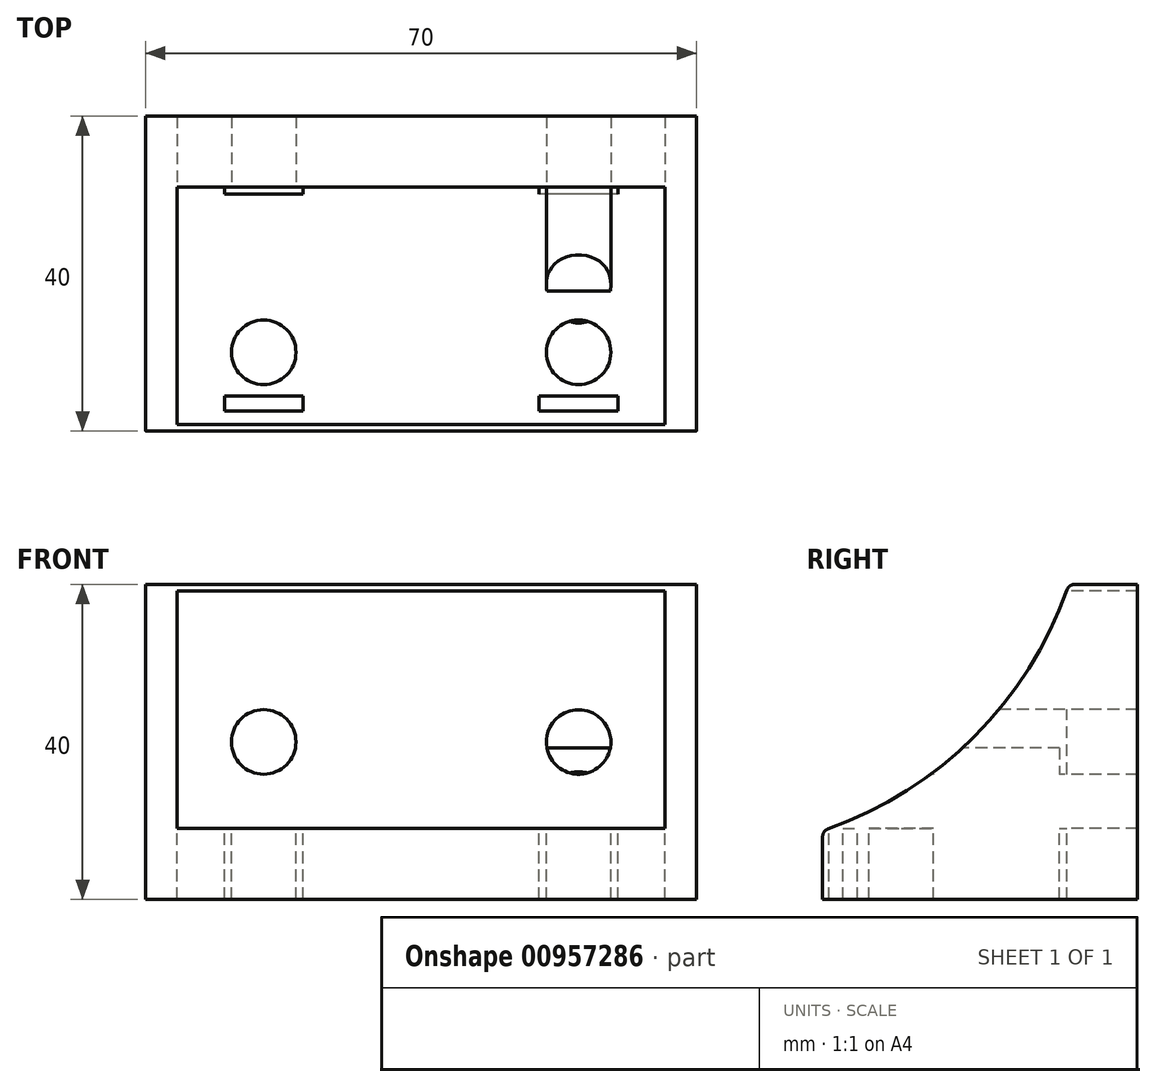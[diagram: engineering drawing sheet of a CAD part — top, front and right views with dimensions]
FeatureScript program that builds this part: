
annotation { "Feature Type Name" : "Feature", "Feature Type Description" : "" }
export const myFeature = defineFeature(function(context is Context, id is Id, definition is map)
    precondition{}
    {
        {
            var Q0;
            Q0=qCreatedBy(makeId("Right.planeOp"),FACE);
            var sketch = newSketch(context, id + "F0", { "sketchPlane" : qUnion([Q0])});
            skLineSegment(sketch, "E0", {"start": v(32.81, -19.75) * mm, "end": v(30.19, -19.75) * mm, "construction": true});
            skLineSegment(sketch, "E1", {"start": v(4.4, -19.75) * mm, "end": v(2.6, -19.75) * mm, "construction": true});
            skLineSegment(sketch, "E2", {"start": v(31, -3.35) * mm, "end": v(40, -3.35) * mm, "construction": true});
            skLineSegment(sketch, "E3", {"start": v(40, 4.85) * mm, "end": v(31, 4.85) * mm, "construction": true});
            skLineSegment(sketch, "E4", {"start": v(5.9, -10.25) * mm, "end": v(5.9, -19.25) * mm, "construction": true});
            skLineSegment(sketch, "E5", {"start": v(14.1, -19.25) * mm, "end": v(14.1, -10.25) * mm, "construction": true});
            skLineSegment(sketch, "E6", {"start": v(31, -10.25) * mm, "end": v(31, 19.92) * mm, "construction": true});
            skLineSegment(sketch, "E7", {"start": v(0.83, -10.25) * mm, "end": v(31, -10.25) * mm, "construction": true});
            skLineSegment(sketch, "E8", {"start": v(40.45, 0.75) * mm, "end": v(30.55, 0.75) * mm, "construction": true});
            skLineSegment(sketch, "E9", {"start": v(10, -19.7) * mm, "end": v(10, -9.8) * mm, "construction": true});
            skLineSegment(sketch, "E10", {"start": v(32.62, -20.84) * mm, "end": v(32.9, -19.25) * mm, "construction": true});
            skLineSegment(sketch, "E11", {"start": v(30.1, -19.25) * mm, "end": v(30.38, -20.84) * mm, "construction": true});
            skLineSegment(sketch, "E12", {"start": v(30.87, -21.25) * mm, "end": v(30.83, -21.25) * mm, "construction": true});
            skLineSegment(sketch, "E13", {"start": v(30.83, -21.25) * mm, "end": v(30.79, -21.24) * mm, "construction": true});
            skLineSegment(sketch, "E14", {"start": v(30.79, -21.24) * mm, "end": v(30.74, -21.23) * mm, "construction": true});
            skLineSegment(sketch, "E15", {"start": v(30.74, -21.23) * mm, "end": v(30.7, -21.22) * mm, "construction": true});
            skLineSegment(sketch, "E16", {"start": v(30.7, -21.22) * mm, "end": v(30.66, -21.2) * mm, "construction": true});
            skLineSegment(sketch, "E17", {"start": v(30.66, -21.2) * mm, "end": v(30.62, -21.18) * mm, "construction": true});
            skLineSegment(sketch, "E18", {"start": v(30.62, -21.18) * mm, "end": v(30.59, -21.16) * mm, "construction": true});
            skLineSegment(sketch, "E19", {"start": v(30.59, -21.16) * mm, "end": v(30.55, -21.13) * mm, "construction": true});
            skLineSegment(sketch, "E20", {"start": v(30.55, -21.13) * mm, "end": v(30.52, -21.1) * mm, "construction": true});
            skLineSegment(sketch, "E21", {"start": v(30.52, -21.1) * mm, "end": v(30.49, -21.07) * mm, "construction": true});
            skLineSegment(sketch, "E22", {"start": v(30.49, -21.07) * mm, "end": v(30.46, -21.04) * mm, "construction": true});
            skLineSegment(sketch, "E23", {"start": v(30.46, -21.04) * mm, "end": v(30.44, -21) * mm, "construction": true});
            skLineSegment(sketch, "E24", {"start": v(30.44, -21) * mm, "end": v(30.42, -20.96) * mm, "construction": true});
            skLineSegment(sketch, "E25", {"start": v(30.42, -20.96) * mm, "end": v(30.4, -20.92) * mm, "construction": true});
            skLineSegment(sketch, "E26", {"start": v(30.4, -20.92) * mm, "end": v(30.39, -20.88) * mm, "construction": true});
            skLineSegment(sketch, "E27", {"start": v(30.39, -20.88) * mm, "end": v(30.38, -20.84) * mm, "construction": true});
            skLineSegment(sketch, "E28", {"start": v(30.87, -21.25) * mm, "end": v(32.13, -21.25) * mm, "construction": true});
            skLineSegment(sketch, "E29", {"start": v(32.62, -20.84) * mm, "end": v(32.61, -20.88) * mm, "construction": true});
            skLineSegment(sketch, "E30", {"start": v(32.61, -20.88) * mm, "end": v(32.6, -20.92) * mm, "construction": true});
            skLineSegment(sketch, "E31", {"start": v(32.6, -20.92) * mm, "end": v(32.58, -20.96) * mm, "construction": true});
            skLineSegment(sketch, "E32", {"start": v(32.58, -20.96) * mm, "end": v(32.56, -21) * mm, "construction": true});
            skLineSegment(sketch, "E33", {"start": v(32.56, -21) * mm, "end": v(32.54, -21.04) * mm, "construction": true});
            skLineSegment(sketch, "E34", {"start": v(32.54, -21.04) * mm, "end": v(32.51, -21.07) * mm, "construction": true});
            skLineSegment(sketch, "E35", {"start": v(32.51, -21.07) * mm, "end": v(32.48, -21.1) * mm, "construction": true});
            skLineSegment(sketch, "E36", {"start": v(32.48, -21.1) * mm, "end": v(32.45, -21.13) * mm, "construction": true});
            skLineSegment(sketch, "E37", {"start": v(32.45, -21.13) * mm, "end": v(32.41, -21.16) * mm, "construction": true});
            skLineSegment(sketch, "E38", {"start": v(32.41, -21.16) * mm, "end": v(32.38, -21.18) * mm, "construction": true});
            skLineSegment(sketch, "E39", {"start": v(32.38, -21.18) * mm, "end": v(32.34, -21.2) * mm, "construction": true});
            skLineSegment(sketch, "E40", {"start": v(32.34, -21.2) * mm, "end": v(32.3, -21.22) * mm, "construction": true});
            skLineSegment(sketch, "E41", {"start": v(32.3, -21.22) * mm, "end": v(32.26, -21.23) * mm, "construction": true});
            skLineSegment(sketch, "E42", {"start": v(32.26, -21.23) * mm, "end": v(32.21, -21.24) * mm, "construction": true});
            skLineSegment(sketch, "E43", {"start": v(32.21, -21.24) * mm, "end": v(32.17, -21.25) * mm, "construction": true});
            skLineSegment(sketch, "E44", {"start": v(32.17, -21.25) * mm, "end": v(32.13, -21.25) * mm, "construction": true});
            skLineSegment(sketch, "E45", {"start": v(2.55, -19.25) * mm, "end": v(2.69, -20.8) * mm, "construction": true});
            skLineSegment(sketch, "E46", {"start": v(4.31, -20.8) * mm, "end": v(4.45, -19.25) * mm, "construction": true});
            skLineSegment(sketch, "E47", {"start": v(3.18, -21.25) * mm, "end": v(3.14, -21.25) * mm, "construction": true});
            skLineSegment(sketch, "E48", {"start": v(3.14, -21.25) * mm, "end": v(3.1, -21.24) * mm, "construction": true});
            skLineSegment(sketch, "E49", {"start": v(3.1, -21.24) * mm, "end": v(3.05, -21.23) * mm, "construction": true});
            skLineSegment(sketch, "E50", {"start": v(3.05, -21.23) * mm, "end": v(3.01, -21.22) * mm, "construction": true});
            skLineSegment(sketch, "E51", {"start": v(3.01, -21.22) * mm, "end": v(2.97, -21.2) * mm, "construction": true});
            skLineSegment(sketch, "E52", {"start": v(2.97, -21.2) * mm, "end": v(2.93, -21.18) * mm, "construction": true});
            skLineSegment(sketch, "E53", {"start": v(2.93, -21.18) * mm, "end": v(2.9, -21.16) * mm, "construction": true});
            skLineSegment(sketch, "E54", {"start": v(2.9, -21.16) * mm, "end": v(2.86, -21.13) * mm, "construction": true});
            skLineSegment(sketch, "E55", {"start": v(2.86, -21.13) * mm, "end": v(2.83, -21.1) * mm, "construction": true});
            skLineSegment(sketch, "E56", {"start": v(2.83, -21.1) * mm, "end": v(2.8, -21.07) * mm, "construction": true});
            skLineSegment(sketch, "E57", {"start": v(2.8, -21.07) * mm, "end": v(2.77, -21.04) * mm, "construction": true});
            skLineSegment(sketch, "E58", {"start": v(2.77, -21.04) * mm, "end": v(2.75, -21) * mm, "construction": true});
            skLineSegment(sketch, "E59", {"start": v(2.75, -21) * mm, "end": v(2.73, -20.96) * mm, "construction": true});
            skLineSegment(sketch, "E60", {"start": v(2.73, -20.96) * mm, "end": v(2.71, -20.92) * mm, "construction": true});
            skLineSegment(sketch, "E61", {"start": v(2.71, -20.92) * mm, "end": v(2.7, -20.88) * mm, "construction": true});
            skLineSegment(sketch, "E62", {"start": v(2.7, -20.88) * mm, "end": v(2.7, -20.84) * mm, "construction": true});
            skLineSegment(sketch, "E63", {"start": v(2.7, -20.84) * mm, "end": v(2.69, -20.8) * mm, "construction": true});
            skLineSegment(sketch, "E64", {"start": v(3.18, -21.25) * mm, "end": v(3.82, -21.25) * mm, "construction": true});
            skLineSegment(sketch, "E65", {"start": v(4.31, -20.8) * mm, "end": v(4.3, -20.84) * mm, "construction": true});
            skLineSegment(sketch, "E66", {"start": v(4.3, -20.84) * mm, "end": v(4.3, -20.88) * mm, "construction": true});
            skLineSegment(sketch, "E67", {"start": v(4.3, -20.88) * mm, "end": v(4.29, -20.92) * mm, "construction": true});
            skLineSegment(sketch, "E68", {"start": v(4.29, -20.92) * mm, "end": v(4.27, -20.96) * mm, "construction": true});
            skLineSegment(sketch, "E69", {"start": v(4.27, -20.96) * mm, "end": v(4.25, -21) * mm, "construction": true});
            skLineSegment(sketch, "E70", {"start": v(4.25, -21) * mm, "end": v(4.23, -21.04) * mm, "construction": true});
            skLineSegment(sketch, "E71", {"start": v(4.23, -21.04) * mm, "end": v(4.2, -21.07) * mm, "construction": true});
            skLineSegment(sketch, "E72", {"start": v(4.2, -21.07) * mm, "end": v(4.17, -21.1) * mm, "construction": true});
            skLineSegment(sketch, "E73", {"start": v(4.17, -21.1) * mm, "end": v(4.14, -21.13) * mm, "construction": true});
            skLineSegment(sketch, "E74", {"start": v(4.14, -21.13) * mm, "end": v(4.1, -21.16) * mm, "construction": true});
            skLineSegment(sketch, "E75", {"start": v(4.1, -21.16) * mm, "end": v(4.07, -21.18) * mm, "construction": true});
            skLineSegment(sketch, "E76", {"start": v(4.07, -21.18) * mm, "end": v(4.03, -21.2) * mm, "construction": true});
            skLineSegment(sketch, "E77", {"start": v(4.03, -21.2) * mm, "end": v(3.99, -21.22) * mm, "construction": true});
            skLineSegment(sketch, "E78", {"start": v(3.99, -21.22) * mm, "end": v(3.95, -21.23) * mm, "construction": true});
            skLineSegment(sketch, "E79", {"start": v(3.95, -21.23) * mm, "end": v(3.9, -21.24) * mm, "construction": true});
            skLineSegment(sketch, "E80", {"start": v(3.9, -21.24) * mm, "end": v(3.86, -21.25) * mm, "construction": true});
            skLineSegment(sketch, "E81", {"start": v(3.86, -21.25) * mm, "end": v(3.82, -21.25) * mm, "construction": true});
            skLineSegment(sketch, "E82", {"start": v(30.37, -20.78) * mm, "end": v(32.63, -20.78) * mm, "construction": true});
            skLineSegment(sketch, "E83", {"start": v(2.68, -20.78) * mm, "end": v(4.32, -20.78) * mm, "construction": true});
            skLineSegment(sketch, "E84", {"start": v(0, -11.25) * mm, "end": v(0, -19.25) * mm});
            skLineSegment(sketch, "E85", {"start": v(40, -19.25) * mm, "end": v(40, 20.75) * mm});
            skArc(sketch, "E86", {"start": v(0.67, -10.3) * mm, "mid": v(0.18, -10.67) * mm, "end": v(0, -11.25) * mm});
            skLineSegment(sketch, "E87", {"start": v(40, 20.75) * mm, "end": v(32, 20.75) * mm});
            skArc(sketch, "E88", {"start": v(32, 20.75) * mm, "mid": v(31.42, 20.57) * mm, "end": v(31.06, 20.08) * mm});
            skArc(sketch, "E89", {"start": v(0.67, -10.3) * mm, "mid": v(19.3, 1.46) * mm, "end": v(31.06, 20.08) * mm});
            skLineSegment(sketch, "E90", {"start": v(40, -19.25) * mm, "end": v(0, -19.25) * mm});
            skSolve(sketch);
        }
        {
            var Q0;
            Q0=makeQuery(id+"F0.imprint","IMPRINT",FACE,{"disambiguationData":[TD([[makeQuery(id+"F0.imprint","IMPRINT",EDGE,{"derivedFrom":sQuery(id+"F0.wireOp",EDGE,"E84")}),1.0]])]});
            extrude(context, id + "F1", {"entities" : qUnion([Q0]), "endBound" : BoundingType.SYMMETRIC, "depth" : 70 * mm, "offsetDistance" : 25 * mm});
        }
        {
            var Q0;
            Q0=qCreatedBy(makeId("Front.planeOp"),FACE);
            var sketch = newSketch(context, id + "F2", { "sketchPlane" : qUnion([Q0])});
            skLineSegment(sketch, "E91", {"start": v(17.26, -20.84) * mm, "end": v(15.09, -20.84) * mm});
            skLineSegment(sketch, "E92", {"start": v(22.7, -20.8) * mm, "end": v(22.74, -20.84) * mm});
            skLineSegment(sketch, "E93", {"start": v(17.26, -20.84) * mm, "end": v(17.3, -20.8) * mm});
            skLineSegment(sketch, "E94", {"start": v(24.91, -20.84) * mm, "end": v(22.74, -20.84) * mm});
            skLineSegment(sketch, "E95", {"start": v(-22.74, -20.84) * mm, "end": v(-24.91, -20.84) * mm});
            skLineSegment(sketch, "E96", {"start": v(-17.3, -20.8) * mm, "end": v(-17.26, -20.84) * mm});
            skLineSegment(sketch, "E97", {"start": v(-22.74, -20.84) * mm, "end": v(-22.7, -20.8) * mm});
            skLineSegment(sketch, "E98", {"start": v(-15.09, -20.84) * mm, "end": v(-17.26, -20.84) * mm});
            skLineSegment(sketch, "E99", {"start": v(-24.1, -10.25) * mm, "end": v(-24.1, -19.25) * mm});
            skLineSegment(sketch, "E100", {"start": v(-15.9, -19.25) * mm, "end": v(-15.9, -10.25) * mm});
            skLineSegment(sketch, "E101", {"start": v(15.9, -10.25) * mm, "end": v(15.9, -19.25) * mm});
            skLineSegment(sketch, "E102", {"start": v(24.1, -19.25) * mm, "end": v(24.1, -10.25) * mm});
            skLineSegment(sketch, "E103", {"start": v(-24.3, 0.75) * mm, "end": v(-15.7, 0.75) * mm, "construction": true});
            skLineSegment(sketch, "E104", {"start": v(-20, -3.55) * mm, "end": v(-20, 5.06) * mm, "construction": true});
            skLineSegment(sketch, "E105", {"start": v(15.7, 0.75) * mm, "end": v(24.3, 0.75) * mm, "construction": true});
            skLineSegment(sketch, "E106", {"start": v(20, -3.55) * mm, "end": v(20, 5.06) * mm, "construction": true});
            skLineSegment(sketch, "E107", {"start": v(20, -19.7) * mm, "end": v(20, -9.8) * mm});
            skLineSegment(sketch, "E108", {"start": v(-20, -19.7) * mm, "end": v(-20, -9.8) * mm});
            skLineSegment(sketch, "E109", {"start": v(35, 20.75) * mm, "end": v(-35, 20.75) * mm});
            skCircle(sketch, "E110", {"center": v(-20, 0.75) * mm, "radius": 4.1 * mm});
            skCircle(sketch, "E111", {"center": v(20, 0.75) * mm, "radius": 4.1 * mm});
            skLineSegment(sketch, "E112", {"start": v(23.12, -21.25) * mm, "end": v(23.1, -21.23) * mm});
            skLineSegment(sketch, "E113", {"start": v(23.1, -21.23) * mm, "end": v(23.06, -21.18) * mm});
            skLineSegment(sketch, "E114", {"start": v(23.06, -21.18) * mm, "end": v(23, -21.1) * mm});
            skLineSegment(sketch, "E115", {"start": v(23, -21.1) * mm, "end": v(22.85, -20.95) * mm});
            skLineSegment(sketch, "E116", {"start": v(22.85, -20.95) * mm, "end": v(22.7, -20.8) * mm});
            skLineSegment(sketch, "E117", {"start": v(24.42, -21.25) * mm, "end": v(24.46, -21.25) * mm});
            skLineSegment(sketch, "E118", {"start": v(24.46, -21.25) * mm, "end": v(24.5, -21.24) * mm});
            skLineSegment(sketch, "E119", {"start": v(24.5, -21.24) * mm, "end": v(24.55, -21.23) * mm});
            skLineSegment(sketch, "E120", {"start": v(24.55, -21.23) * mm, "end": v(24.6, -21.22) * mm});
            skLineSegment(sketch, "E121", {"start": v(24.6, -21.22) * mm, "end": v(24.63, -21.2) * mm});
            skLineSegment(sketch, "E122", {"start": v(24.63, -21.2) * mm, "end": v(24.67, -21.18) * mm});
            skLineSegment(sketch, "E123", {"start": v(24.67, -21.18) * mm, "end": v(24.7, -21.16) * mm});
            skLineSegment(sketch, "E124", {"start": v(24.7, -21.16) * mm, "end": v(24.74, -21.13) * mm});
            skLineSegment(sketch, "E125", {"start": v(24.74, -21.13) * mm, "end": v(24.77, -21.1) * mm});
            skLineSegment(sketch, "E126", {"start": v(24.77, -21.1) * mm, "end": v(24.8, -21.07) * mm});
            skLineSegment(sketch, "E127", {"start": v(24.8, -21.07) * mm, "end": v(24.83, -21.04) * mm});
            skLineSegment(sketch, "E128", {"start": v(24.83, -21.04) * mm, "end": v(24.85, -21) * mm});
            skLineSegment(sketch, "E129", {"start": v(24.85, -21) * mm, "end": v(24.87, -20.96) * mm});
            skLineSegment(sketch, "E130", {"start": v(24.87, -20.96) * mm, "end": v(24.9, -20.92) * mm});
            skLineSegment(sketch, "E131", {"start": v(24.9, -20.92) * mm, "end": v(24.9, -20.88) * mm});
            skLineSegment(sketch, "E132", {"start": v(24.9, -20.88) * mm, "end": v(24.91, -20.84) * mm});
            skLineSegment(sketch, "E133", {"start": v(24.91, -20.84) * mm, "end": v(24.92, -20.8) * mm});
            skLineSegment(sketch, "E134", {"start": v(24.42, -21.25) * mm, "end": v(23.12, -21.25) * mm});
            skLineSegment(sketch, "E135", {"start": v(-22.7, -20.8) * mm, "end": v(-22.87, -20.97) * mm});
            skLineSegment(sketch, "E136", {"start": v(-22.87, -20.97) * mm, "end": v(-23, -21.1) * mm});
            skLineSegment(sketch, "E137", {"start": v(-23, -21.1) * mm, "end": v(-23.08, -21.2) * mm});
            skLineSegment(sketch, "E138", {"start": v(-23.08, -21.2) * mm, "end": v(-23.11, -21.24) * mm});
            skLineSegment(sketch, "E139", {"start": v(-23.11, -21.24) * mm, "end": v(-23.12, -21.25) * mm});
            skLineSegment(sketch, "E140", {"start": v(-24.92, -20.8) * mm, "end": v(-24.91, -20.84) * mm});
            skLineSegment(sketch, "E141", {"start": v(-24.91, -20.84) * mm, "end": v(-24.9, -20.88) * mm});
            skLineSegment(sketch, "E142", {"start": v(-24.9, -20.88) * mm, "end": v(-24.9, -20.92) * mm});
            skLineSegment(sketch, "E143", {"start": v(-24.9, -20.92) * mm, "end": v(-24.87, -20.96) * mm});
            skLineSegment(sketch, "E144", {"start": v(-24.87, -20.96) * mm, "end": v(-24.85, -21) * mm});
            skLineSegment(sketch, "E145", {"start": v(-24.85, -21) * mm, "end": v(-24.83, -21.04) * mm});
            skLineSegment(sketch, "E146", {"start": v(-24.83, -21.04) * mm, "end": v(-24.8, -21.07) * mm});
            skLineSegment(sketch, "E147", {"start": v(-24.8, -21.07) * mm, "end": v(-24.77, -21.1) * mm});
            skLineSegment(sketch, "E148", {"start": v(-24.77, -21.1) * mm, "end": v(-24.74, -21.13) * mm});
            skLineSegment(sketch, "E149", {"start": v(-24.74, -21.13) * mm, "end": v(-24.7, -21.16) * mm});
            skLineSegment(sketch, "E150", {"start": v(-24.7, -21.16) * mm, "end": v(-24.67, -21.18) * mm});
            skLineSegment(sketch, "E151", {"start": v(-24.67, -21.18) * mm, "end": v(-24.63, -21.2) * mm});
            skLineSegment(sketch, "E152", {"start": v(-24.63, -21.2) * mm, "end": v(-24.6, -21.22) * mm});
            skLineSegment(sketch, "E153", {"start": v(-24.6, -21.22) * mm, "end": v(-24.55, -21.23) * mm});
            skLineSegment(sketch, "E154", {"start": v(-24.55, -21.23) * mm, "end": v(-24.5, -21.24) * mm});
            skLineSegment(sketch, "E155", {"start": v(-24.5, -21.24) * mm, "end": v(-24.46, -21.25) * mm});
            skLineSegment(sketch, "E156", {"start": v(-24.46, -21.25) * mm, "end": v(-24.42, -21.25) * mm});
            skLineSegment(sketch, "E157", {"start": v(-23.12, -21.25) * mm, "end": v(-24.42, -21.25) * mm});
            skLineSegment(sketch, "E158", {"start": v(-16.88, -21.25) * mm, "end": v(-16.9, -21.23) * mm});
            skLineSegment(sketch, "E159", {"start": v(-16.9, -21.23) * mm, "end": v(-16.94, -21.18) * mm});
            skLineSegment(sketch, "E160", {"start": v(-16.94, -21.18) * mm, "end": v(-17, -21.1) * mm});
            skLineSegment(sketch, "E161", {"start": v(-17, -21.1) * mm, "end": v(-17.15, -20.95) * mm});
            skLineSegment(sketch, "E162", {"start": v(-17.15, -20.95) * mm, "end": v(-17.3, -20.8) * mm});
            skLineSegment(sketch, "E163", {"start": v(-15.58, -21.25) * mm, "end": v(-15.54, -21.25) * mm});
            skLineSegment(sketch, "E164", {"start": v(-15.54, -21.25) * mm, "end": v(-15.5, -21.24) * mm});
            skLineSegment(sketch, "E165", {"start": v(-15.5, -21.24) * mm, "end": v(-15.45, -21.23) * mm});
            skLineSegment(sketch, "E166", {"start": v(-15.45, -21.23) * mm, "end": v(-15.4, -21.22) * mm});
            skLineSegment(sketch, "E167", {"start": v(-15.4, -21.22) * mm, "end": v(-15.37, -21.2) * mm});
            skLineSegment(sketch, "E168", {"start": v(-15.37, -21.2) * mm, "end": v(-15.33, -21.18) * mm});
            skLineSegment(sketch, "E169", {"start": v(-15.33, -21.18) * mm, "end": v(-15.3, -21.16) * mm});
            skLineSegment(sketch, "E170", {"start": v(-15.3, -21.16) * mm, "end": v(-15.26, -21.13) * mm});
            skLineSegment(sketch, "E171", {"start": v(-15.26, -21.13) * mm, "end": v(-15.23, -21.1) * mm});
            skLineSegment(sketch, "E172", {"start": v(-15.23, -21.1) * mm, "end": v(-15.2, -21.07) * mm});
            skLineSegment(sketch, "E173", {"start": v(-15.2, -21.07) * mm, "end": v(-15.17, -21.04) * mm});
            skLineSegment(sketch, "E174", {"start": v(-15.17, -21.04) * mm, "end": v(-15.15, -21) * mm});
            skLineSegment(sketch, "E175", {"start": v(-15.15, -21) * mm, "end": v(-15.13, -20.96) * mm});
            skLineSegment(sketch, "E176", {"start": v(-15.13, -20.96) * mm, "end": v(-15.1, -20.92) * mm});
            skLineSegment(sketch, "E177", {"start": v(-15.1, -20.92) * mm, "end": v(-15.1, -20.88) * mm});
            skLineSegment(sketch, "E178", {"start": v(-15.1, -20.88) * mm, "end": v(-15.09, -20.84) * mm});
            skLineSegment(sketch, "E179", {"start": v(-15.09, -20.84) * mm, "end": v(-15.08, -20.8) * mm});
            skLineSegment(sketch, "E180", {"start": v(-15.58, -21.25) * mm, "end": v(-16.88, -21.25) * mm});
            skLineSegment(sketch, "E181", {"start": v(17.3, -20.8) * mm, "end": v(17.13, -20.97) * mm});
            skLineSegment(sketch, "E182", {"start": v(17.13, -20.97) * mm, "end": v(17, -21.1) * mm});
            skLineSegment(sketch, "E183", {"start": v(17, -21.1) * mm, "end": v(16.92, -21.2) * mm});
            skLineSegment(sketch, "E184", {"start": v(16.92, -21.2) * mm, "end": v(16.89, -21.24) * mm});
            skLineSegment(sketch, "E185", {"start": v(16.89, -21.24) * mm, "end": v(16.88, -21.25) * mm});
            skLineSegment(sketch, "E186", {"start": v(15.08, -20.8) * mm, "end": v(15.09, -20.84) * mm});
            skLineSegment(sketch, "E187", {"start": v(15.09, -20.84) * mm, "end": v(15.1, -20.88) * mm});
            skLineSegment(sketch, "E188", {"start": v(15.1, -20.88) * mm, "end": v(15.1, -20.92) * mm});
            skLineSegment(sketch, "E189", {"start": v(15.1, -20.92) * mm, "end": v(15.13, -20.96) * mm});
            skLineSegment(sketch, "E190", {"start": v(15.13, -20.96) * mm, "end": v(15.15, -21) * mm});
            skLineSegment(sketch, "E191", {"start": v(15.15, -21) * mm, "end": v(15.17, -21.04) * mm});
            skLineSegment(sketch, "E192", {"start": v(15.17, -21.04) * mm, "end": v(15.2, -21.07) * mm});
            skLineSegment(sketch, "E193", {"start": v(15.2, -21.07) * mm, "end": v(15.23, -21.1) * mm});
            skLineSegment(sketch, "E194", {"start": v(15.23, -21.1) * mm, "end": v(15.26, -21.13) * mm});
            skLineSegment(sketch, "E195", {"start": v(15.26, -21.13) * mm, "end": v(15.3, -21.16) * mm});
            skLineSegment(sketch, "E196", {"start": v(15.3, -21.16) * mm, "end": v(15.33, -21.18) * mm});
            skLineSegment(sketch, "E197", {"start": v(15.33, -21.18) * mm, "end": v(15.37, -21.2) * mm});
            skLineSegment(sketch, "E198", {"start": v(15.37, -21.2) * mm, "end": v(15.4, -21.22) * mm});
            skLineSegment(sketch, "E199", {"start": v(15.4, -21.22) * mm, "end": v(15.45, -21.23) * mm});
            skLineSegment(sketch, "E200", {"start": v(15.45, -21.23) * mm, "end": v(15.5, -21.24) * mm});
            skLineSegment(sketch, "E201", {"start": v(15.5, -21.24) * mm, "end": v(15.54, -21.25) * mm});
            skLineSegment(sketch, "E202", {"start": v(15.54, -21.25) * mm, "end": v(15.58, -21.25) * mm});
            skLineSegment(sketch, "E203", {"start": v(16.88, -21.25) * mm, "end": v(15.58, -21.25) * mm});
            skLineSegment(sketch, "E204", {"start": v(24.92, -20.78) * mm, "end": v(24.92, -20.8) * mm});
            skLineSegment(sketch, "E205", {"start": v(24.92, -20.78) * mm, "end": v(25, -19.25) * mm});
            skLineSegment(sketch, "E206", {"start": v(15, -19.25) * mm, "end": v(15.08, -20.78) * mm});
            skLineSegment(sketch, "E207", {"start": v(15.08, -20.8) * mm, "end": v(15.08, -20.78) * mm});
            skLineSegment(sketch, "E208", {"start": v(17.3, -20.8) * mm, "end": v(15.08, -20.8) * mm});
            skLineSegment(sketch, "E209", {"start": v(17.3, -20.8) * mm, "end": v(17.57, -20.57) * mm});
            skLineSegment(sketch, "E210", {"start": v(17.57, -20.57) * mm, "end": v(17.86, -20.37) * mm});
            skLineSegment(sketch, "E211", {"start": v(17.86, -20.37) * mm, "end": v(18.16, -20.2) * mm});
            skLineSegment(sketch, "E212", {"start": v(18.16, -20.2) * mm, "end": v(18.48, -20.05) * mm});
            skLineSegment(sketch, "E213", {"start": v(18.48, -20.05) * mm, "end": v(18.8, -19.93) * mm});
            skLineSegment(sketch, "E214", {"start": v(18.8, -19.93) * mm, "end": v(19.14, -19.84) * mm});
            skLineSegment(sketch, "E215", {"start": v(19.14, -19.84) * mm, "end": v(19.49, -19.78) * mm});
            skLineSegment(sketch, "E216", {"start": v(19.49, -19.78) * mm, "end": v(19.84, -19.75) * mm});
            skLineSegment(sketch, "E217", {"start": v(19.84, -19.75) * mm, "end": v(20.19, -19.75) * mm});
            skLineSegment(sketch, "E218", {"start": v(20.19, -19.75) * mm, "end": v(20.53, -19.79) * mm});
            skLineSegment(sketch, "E219", {"start": v(20.53, -19.79) * mm, "end": v(20.88, -19.85) * mm});
            skLineSegment(sketch, "E220", {"start": v(20.88, -19.85) * mm, "end": v(21.21, -19.94) * mm});
            skLineSegment(sketch, "E221", {"start": v(21.21, -19.94) * mm, "end": v(21.54, -20.06) * mm});
            skLineSegment(sketch, "E222", {"start": v(21.54, -20.06) * mm, "end": v(21.86, -20.2) * mm});
            skLineSegment(sketch, "E223", {"start": v(21.86, -20.2) * mm, "end": v(22.16, -20.38) * mm});
            skLineSegment(sketch, "E224", {"start": v(22.16, -20.38) * mm, "end": v(22.44, -20.58) * mm});
            skLineSegment(sketch, "E225", {"start": v(22.44, -20.58) * mm, "end": v(22.7, -20.8) * mm});
            skLineSegment(sketch, "E226", {"start": v(24.92, -20.8) * mm, "end": v(22.7, -20.8) * mm});
            skLineSegment(sketch, "E227", {"start": v(-15.08, -20.78) * mm, "end": v(-15.08, -20.8) * mm});
            skLineSegment(sketch, "E228", {"start": v(-15.08, -20.78) * mm, "end": v(-15, -19.25) * mm});
            skLineSegment(sketch, "E229", {"start": v(-25, -19.25) * mm, "end": v(-24.92, -20.78) * mm});
            skLineSegment(sketch, "E230", {"start": v(-24.92, -20.8) * mm, "end": v(-24.92, -20.78) * mm});
            skLineSegment(sketch, "E231", {"start": v(-22.7, -20.8) * mm, "end": v(-24.92, -20.8) * mm});
            skLineSegment(sketch, "E232", {"start": v(-22.7, -20.8) * mm, "end": v(-22.43, -20.57) * mm});
            skLineSegment(sketch, "E233", {"start": v(-22.43, -20.57) * mm, "end": v(-22.14, -20.37) * mm});
            skLineSegment(sketch, "E234", {"start": v(-22.14, -20.37) * mm, "end": v(-21.84, -20.2) * mm});
            skLineSegment(sketch, "E235", {"start": v(-21.84, -20.2) * mm, "end": v(-21.52, -20.05) * mm});
            skLineSegment(sketch, "E236", {"start": v(-21.52, -20.05) * mm, "end": v(-21.2, -19.93) * mm});
            skLineSegment(sketch, "E237", {"start": v(-21.2, -19.93) * mm, "end": v(-20.86, -19.84) * mm});
            skLineSegment(sketch, "E238", {"start": v(-20.86, -19.84) * mm, "end": v(-20.51, -19.78) * mm});
            skLineSegment(sketch, "E239", {"start": v(-20.51, -19.78) * mm, "end": v(-20.16, -19.75) * mm});
            skLineSegment(sketch, "E240", {"start": v(-20.16, -19.75) * mm, "end": v(-19.81, -19.75) * mm});
            skLineSegment(sketch, "E241", {"start": v(-19.81, -19.75) * mm, "end": v(-19.47, -19.79) * mm});
            skLineSegment(sketch, "E242", {"start": v(-19.47, -19.79) * mm, "end": v(-19.12, -19.85) * mm});
            skLineSegment(sketch, "E243", {"start": v(-19.12, -19.85) * mm, "end": v(-18.79, -19.94) * mm});
            skLineSegment(sketch, "E244", {"start": v(-18.79, -19.94) * mm, "end": v(-18.46, -20.06) * mm});
            skLineSegment(sketch, "E245", {"start": v(-18.46, -20.06) * mm, "end": v(-18.14, -20.2) * mm});
            skLineSegment(sketch, "E246", {"start": v(-18.14, -20.2) * mm, "end": v(-17.84, -20.38) * mm});
            skLineSegment(sketch, "E247", {"start": v(-17.84, -20.38) * mm, "end": v(-17.56, -20.58) * mm});
            skLineSegment(sketch, "E248", {"start": v(-17.56, -20.58) * mm, "end": v(-17.3, -20.8) * mm});
            skLineSegment(sketch, "E249", {"start": v(-15.08, -20.8) * mm, "end": v(-17.3, -20.8) * mm});
            skLineSegment(sketch, "E250", {"start": v(31, -10.25) * mm, "end": v(31, 19.92) * mm});
            skLineSegment(sketch, "E251", {"start": v(31, -10.25) * mm, "end": v(-31, -10.25) * mm});
            skLineSegment(sketch, "E252", {"start": v(-31, -10.25) * mm, "end": v(-31, 19.92) * mm});
            skLineSegment(sketch, "E253", {"start": v(-31, 19.92) * mm, "end": v(31, 19.92) * mm});
            skLineSegment(sketch, "E254", {"start": v(35, 20.08) * mm, "end": v(-35, 20.08) * mm});
            skLineSegment(sketch, "E255", {"start": v(35, 20.75) * mm, "end": v(35, -19.25) * mm});
            skLineSegment(sketch, "E256", {"start": v(-35, 20.75) * mm, "end": v(-35, -19.25) * mm});
            skLineSegment(sketch, "E257", {"start": v(35, -19.25) * mm, "end": v(-35, -19.25) * mm});
            skLineSegment(sketch, "E258", {"start": v(35, -11.25) * mm, "end": v(-35, -11.25) * mm});
            skLineSegment(sketch, "E259", {"start": v(35, -10.3) * mm, "end": v(-35, -10.3) * mm});
            skSolve(sketch);
        }
        {
            var Q0;
            Q0=makeQuery(id+"F2.imprint","IMPRINT",FACE,{"disambiguationData":[TD([[makeQuery(id+"F2.imprint","IMPRINT",EDGE,{"derivedFrom":sQuery(id+"F2.wireOp",EDGE,"E110")}),1.0]])]});
            var Q1;
            Q1=makeQuery(id+"F2.imprint","IMPRINT",FACE,{"disambiguationData":[TD([[makeQuery(id+"F2.imprint","IMPRINT",EDGE,{"derivedFrom":sQuery(id+"F2.wireOp",EDGE,"E110")}),-1.0]])]});
            var Q2;
            Q2=makeQuery(id+"F2.imprint","IMPRINT",FACE,{"disambiguationData":[TD([[makeQuery(id+"F2.imprint","IMPRINT",EDGE,{"derivedFrom":sQuery(id+"F2.wireOp",EDGE,"E111")}),-1.0]])]});
            extrude(context, id + "F3", {"entities" : qUnion([Q0, Q1, Q2]), "operationType" : NewBodyOperationType.REMOVE, "oppositeDirection" : true, "depth" : 31 * mm, "offsetDistance" : 25 * mm});
        }
        {
            var Q0;
            Q0=makeQuery(id+"F2.imprint","IMPRINT",FACE,{"disambiguationData":[TD([[makeQuery(id+"F2.imprint","IMPRINT",EDGE,{"derivedFrom":sQuery(id+"F2.wireOp",EDGE,"E111")}),-1.0]])]});
            var Q1;
            Q1=makeQuery(id+"F2.imprint","IMPRINT",FACE,{"disambiguationData":[TD([[makeQuery(id+"F2.imprint","IMPRINT",EDGE,{"derivedFrom":sQuery(id+"F2.wireOp",EDGE,"E110")}),-1.0]])]});
            extrude(context, id + "F4", {"entities" : qUnion([Q0, Q1]), "operationType" : NewBodyOperationType.REMOVE, "endBound" : BoundingType.THROUGH_ALL, "oppositeDirection" : true, "depth" : 25 * mm, "offsetDistance" : 25 * mm});
        }
        {
            var Q0;
            Q0=qCreatedBy(makeId("Top.planeOp"),FACE);
            var sketch = newSketch(context, id + "F5", { "sketchPlane" : qUnion([Q0])});
            skLineSegment(sketch, "E260", {"start": v(23.12, 30.87) * mm, "end": v(23.12, 32.13) * mm});
            skLineSegment(sketch, "E261", {"start": v(24.42, 30.87) * mm, "end": v(24.42, 32.13) * mm});
            skLineSegment(sketch, "E262", {"start": v(24.42, 30.87) * mm, "end": v(23.12, 30.87) * mm});
            skLineSegment(sketch, "E263", {"start": v(24.42, 32.13) * mm, "end": v(23.12, 32.13) * mm});
            skLineSegment(sketch, "E264", {"start": v(-16.88, 30.87) * mm, "end": v(-16.88, 32.13) * mm});
            skLineSegment(sketch, "E265", {"start": v(-15.58, 30.87) * mm, "end": v(-15.58, 32.13) * mm});
            skLineSegment(sketch, "E266", {"start": v(-15.58, 30.87) * mm, "end": v(-16.88, 30.87) * mm});
            skLineSegment(sketch, "E267", {"start": v(-15.58, 32.13) * mm, "end": v(-16.88, 32.13) * mm});
            skLineSegment(sketch, "E268", {"start": v(-23.12, 30.87) * mm, "end": v(-23.12, 32.13) * mm});
            skLineSegment(sketch, "E269", {"start": v(-24.42, 30.87) * mm, "end": v(-24.42, 32.13) * mm});
            skLineSegment(sketch, "E270", {"start": v(-23.12, 30.87) * mm, "end": v(-24.42, 30.87) * mm});
            skLineSegment(sketch, "E271", {"start": v(-23.12, 32.13) * mm, "end": v(-24.42, 32.13) * mm});
            skLineSegment(sketch, "E272", {"start": v(16.88, 30.87) * mm, "end": v(16.88, 32.13) * mm});
            skLineSegment(sketch, "E273", {"start": v(15.58, 30.87) * mm, "end": v(15.58, 32.13) * mm});
            skLineSegment(sketch, "E274", {"start": v(16.88, 30.87) * mm, "end": v(15.58, 30.87) * mm});
            skLineSegment(sketch, "E275", {"start": v(16.88, 32.13) * mm, "end": v(15.58, 32.13) * mm});
            skLineSegment(sketch, "E276", {"start": v(23.12, 3.18) * mm, "end": v(23.12, 3.82) * mm});
            skLineSegment(sketch, "E277", {"start": v(24.42, 3.18) * mm, "end": v(24.42, 3.82) * mm});
            skLineSegment(sketch, "E278", {"start": v(24.42, 3.82) * mm, "end": v(23.12, 3.82) * mm});
            skLineSegment(sketch, "E279", {"start": v(24.42, 3.18) * mm, "end": v(23.12, 3.18) * mm});
            skLineSegment(sketch, "E280", {"start": v(-16.88, 3.18) * mm, "end": v(-16.88, 3.82) * mm});
            skLineSegment(sketch, "E281", {"start": v(-15.58, 3.18) * mm, "end": v(-15.58, 3.82) * mm});
            skLineSegment(sketch, "E282", {"start": v(-15.58, 3.82) * mm, "end": v(-16.88, 3.82) * mm});
            skLineSegment(sketch, "E283", {"start": v(-15.58, 3.18) * mm, "end": v(-16.88, 3.18) * mm});
            skLineSegment(sketch, "E284", {"start": v(-23.12, 3.18) * mm, "end": v(-23.12, 3.82) * mm});
            skLineSegment(sketch, "E285", {"start": v(-24.42, 3.18) * mm, "end": v(-24.42, 3.82) * mm});
            skLineSegment(sketch, "E286", {"start": v(-23.12, 3.82) * mm, "end": v(-24.42, 3.82) * mm});
            skLineSegment(sketch, "E287", {"start": v(-23.12, 3.18) * mm, "end": v(-24.42, 3.18) * mm});
            skLineSegment(sketch, "E288", {"start": v(16.88, 3.18) * mm, "end": v(16.88, 3.82) * mm});
            skLineSegment(sketch, "E289", {"start": v(15.58, 3.18) * mm, "end": v(15.58, 3.82) * mm});
            skLineSegment(sketch, "E290", {"start": v(16.88, 3.82) * mm, "end": v(15.58, 3.82) * mm});
            skLineSegment(sketch, "E291", {"start": v(16.88, 3.18) * mm, "end": v(15.58, 3.18) * mm});
            skLineSegment(sketch, "E292", {"start": v(-15.09, 32.62) * mm, "end": v(-17.26, 32.62) * mm});
            skLineSegment(sketch, "E293", {"start": v(-17.26, 32.62) * mm, "end": v(-17.09, 32.56) * mm});
            skLineSegment(sketch, "E294", {"start": v(-17.09, 32.56) * mm, "end": v(-16.98, 32.45) * mm});
            skLineSegment(sketch, "E295", {"start": v(-16.98, 32.45) * mm, "end": v(-16.91, 32.33) * mm});
            skLineSegment(sketch, "E296", {"start": v(-16.91, 32.33) * mm, "end": v(-16.88, 32.17) * mm});
            skLineSegment(sketch, "E297", {"start": v(-16.88, 32.17) * mm, "end": v(-16.88, 32.13) * mm});
            skLineSegment(sketch, "E298", {"start": v(-15.09, 32.62) * mm, "end": v(-15.58, 32.13) * mm});
            skLineSegment(sketch, "E299", {"start": v(24.91, 32.62) * mm, "end": v(22.74, 32.62) * mm});
            skLineSegment(sketch, "E300", {"start": v(22.74, 32.62) * mm, "end": v(22.91, 32.56) * mm});
            skLineSegment(sketch, "E301", {"start": v(22.91, 32.56) * mm, "end": v(23.02, 32.45) * mm});
            skLineSegment(sketch, "E302", {"start": v(23.02, 32.45) * mm, "end": v(23.09, 32.33) * mm});
            skLineSegment(sketch, "E303", {"start": v(23.09, 32.33) * mm, "end": v(23.12, 32.17) * mm});
            skLineSegment(sketch, "E304", {"start": v(23.12, 32.17) * mm, "end": v(23.12, 32.13) * mm});
            skLineSegment(sketch, "E305", {"start": v(24.91, 32.62) * mm, "end": v(24.42, 32.13) * mm});
            skLineSegment(sketch, "E306", {"start": v(-22.74, 32.62) * mm, "end": v(-24.91, 32.62) * mm});
            skLineSegment(sketch, "E307", {"start": v(-23.12, 32.13) * mm, "end": v(-23.1, 32.27) * mm});
            skLineSegment(sketch, "E308", {"start": v(-23.1, 32.27) * mm, "end": v(-23.06, 32.39) * mm});
            skLineSegment(sketch, "E309", {"start": v(-23.06, 32.39) * mm, "end": v(-23, 32.49) * mm});
            skLineSegment(sketch, "E310", {"start": v(-23, 32.49) * mm, "end": v(-22.86, 32.59) * mm});
            skLineSegment(sketch, "E311", {"start": v(-22.86, 32.59) * mm, "end": v(-22.74, 32.62) * mm});
            skLineSegment(sketch, "E312", {"start": v(-24.42, 32.13) * mm, "end": v(-24.91, 32.62) * mm});
            skLineSegment(sketch, "E313", {"start": v(17.26, 32.62) * mm, "end": v(15.09, 32.62) * mm});
            skLineSegment(sketch, "E314", {"start": v(16.88, 32.13) * mm, "end": v(16.9, 32.27) * mm});
            skLineSegment(sketch, "E315", {"start": v(16.9, 32.27) * mm, "end": v(16.94, 32.39) * mm});
            skLineSegment(sketch, "E316", {"start": v(16.94, 32.39) * mm, "end": v(17, 32.49) * mm});
            skLineSegment(sketch, "E317", {"start": v(17, 32.49) * mm, "end": v(17.14, 32.59) * mm});
            skLineSegment(sketch, "E318", {"start": v(17.14, 32.59) * mm, "end": v(17.26, 32.62) * mm});
            skLineSegment(sketch, "E319", {"start": v(15.58, 32.13) * mm, "end": v(15.09, 32.62) * mm});
            skLineSegment(sketch, "E320", {"start": v(24.91, 30.38) * mm, "end": v(22.74, 30.38) * mm});
            skLineSegment(sketch, "E321", {"start": v(23.12, 30.87) * mm, "end": v(23.1, 30.73) * mm});
            skLineSegment(sketch, "E322", {"start": v(23.1, 30.73) * mm, "end": v(23.06, 30.61) * mm});
            skLineSegment(sketch, "E323", {"start": v(23.06, 30.61) * mm, "end": v(23, 30.51) * mm});
            skLineSegment(sketch, "E324", {"start": v(23, 30.51) * mm, "end": v(22.86, 30.41) * mm});
            skLineSegment(sketch, "E325", {"start": v(22.86, 30.41) * mm, "end": v(22.74, 30.38) * mm});
            skLineSegment(sketch, "E326", {"start": v(24.42, 30.87) * mm, "end": v(24.91, 30.38) * mm});
            skLineSegment(sketch, "E327", {"start": v(-15.09, 30.38) * mm, "end": v(-17.26, 30.38) * mm});
            skLineSegment(sketch, "E328", {"start": v(-16.88, 30.87) * mm, "end": v(-16.9, 30.73) * mm});
            skLineSegment(sketch, "E329", {"start": v(-16.9, 30.73) * mm, "end": v(-16.94, 30.61) * mm});
            skLineSegment(sketch, "E330", {"start": v(-16.94, 30.61) * mm, "end": v(-17, 30.51) * mm});
            skLineSegment(sketch, "E331", {"start": v(-17, 30.51) * mm, "end": v(-17.14, 30.41) * mm});
            skLineSegment(sketch, "E332", {"start": v(-17.14, 30.41) * mm, "end": v(-17.26, 30.38) * mm});
            skLineSegment(sketch, "E333", {"start": v(-15.58, 30.87) * mm, "end": v(-15.09, 30.38) * mm});
            skLineSegment(sketch, "E334", {"start": v(-22.74, 30.38) * mm, "end": v(-24.91, 30.38) * mm});
            skLineSegment(sketch, "E335", {"start": v(-22.74, 30.38) * mm, "end": v(-22.91, 30.44) * mm});
            skLineSegment(sketch, "E336", {"start": v(-22.91, 30.44) * mm, "end": v(-23.02, 30.55) * mm});
            skLineSegment(sketch, "E337", {"start": v(-23.02, 30.55) * mm, "end": v(-23.09, 30.67) * mm});
            skLineSegment(sketch, "E338", {"start": v(-23.09, 30.67) * mm, "end": v(-23.12, 30.83) * mm});
            skLineSegment(sketch, "E339", {"start": v(-23.12, 30.83) * mm, "end": v(-23.12, 30.87) * mm});
            skLineSegment(sketch, "E340", {"start": v(-24.91, 30.38) * mm, "end": v(-24.42, 30.87) * mm});
            skLineSegment(sketch, "E341", {"start": v(17.26, 30.38) * mm, "end": v(15.09, 30.38) * mm});
            skLineSegment(sketch, "E342", {"start": v(17.26, 30.38) * mm, "end": v(17.09, 30.44) * mm});
            skLineSegment(sketch, "E343", {"start": v(17.09, 30.44) * mm, "end": v(16.98, 30.55) * mm});
            skLineSegment(sketch, "E344", {"start": v(16.98, 30.55) * mm, "end": v(16.91, 30.67) * mm});
            skLineSegment(sketch, "E345", {"start": v(16.91, 30.67) * mm, "end": v(16.88, 30.83) * mm});
            skLineSegment(sketch, "E346", {"start": v(16.88, 30.83) * mm, "end": v(16.88, 30.87) * mm});
            skLineSegment(sketch, "E347", {"start": v(15.09, 30.38) * mm, "end": v(15.58, 30.87) * mm});
            skLineSegment(sketch, "E348", {"start": v(-22.7, 2.69) * mm, "end": v(-24.92, 2.69) * mm});
            skLineSegment(sketch, "E349", {"start": v(-22.7, 2.69) * mm, "end": v(-22.87, 2.73) * mm});
            skLineSegment(sketch, "E350", {"start": v(-22.87, 2.73) * mm, "end": v(-23, 2.83) * mm});
            skLineSegment(sketch, "E351", {"start": v(-23, 2.83) * mm, "end": v(-23.08, 2.95) * mm});
            skLineSegment(sketch, "E352", {"start": v(-23.08, 2.95) * mm, "end": v(-23.11, 3.08) * mm});
            skLineSegment(sketch, "E353", {"start": v(-23.11, 3.08) * mm, "end": v(-23.12, 3.18) * mm});
            skLineSegment(sketch, "E354", {"start": v(-24.92, 2.69) * mm, "end": v(-24.42, 3.18) * mm});
            skLineSegment(sketch, "E355", {"start": v(17.3, 2.69) * mm, "end": v(15.08, 2.69) * mm});
            skLineSegment(sketch, "E356", {"start": v(17.3, 2.69) * mm, "end": v(17.13, 2.73) * mm});
            skLineSegment(sketch, "E357", {"start": v(17.13, 2.73) * mm, "end": v(17, 2.83) * mm});
            skLineSegment(sketch, "E358", {"start": v(17, 2.83) * mm, "end": v(16.92, 2.95) * mm});
            skLineSegment(sketch, "E359", {"start": v(16.92, 2.95) * mm, "end": v(16.89, 3.08) * mm});
            skLineSegment(sketch, "E360", {"start": v(16.89, 3.08) * mm, "end": v(16.88, 3.18) * mm});
            skLineSegment(sketch, "E361", {"start": v(15.08, 2.69) * mm, "end": v(15.58, 3.18) * mm});
            skLineSegment(sketch, "E362", {"start": v(24.92, 2.69) * mm, "end": v(22.7, 2.69) * mm});
            skLineSegment(sketch, "E363", {"start": v(23.12, 3.18) * mm, "end": v(23.1, 3.05) * mm});
            skLineSegment(sketch, "E364", {"start": v(23.1, 3.05) * mm, "end": v(23.06, 2.92) * mm});
            skLineSegment(sketch, "E365", {"start": v(23.06, 2.92) * mm, "end": v(23, 2.82) * mm});
            skLineSegment(sketch, "E366", {"start": v(23, 2.82) * mm, "end": v(22.86, 2.72) * mm});
            skLineSegment(sketch, "E367", {"start": v(22.86, 2.72) * mm, "end": v(22.7, 2.69) * mm});
            skLineSegment(sketch, "E368", {"start": v(24.42, 3.18) * mm, "end": v(24.92, 2.69) * mm});
            skLineSegment(sketch, "E369", {"start": v(-15.08, 2.69) * mm, "end": v(-17.3, 2.69) * mm});
            skLineSegment(sketch, "E370", {"start": v(-16.88, 3.18) * mm, "end": v(-16.9, 3.05) * mm});
            skLineSegment(sketch, "E371", {"start": v(-16.9, 3.05) * mm, "end": v(-16.94, 2.92) * mm});
            skLineSegment(sketch, "E372", {"start": v(-16.94, 2.92) * mm, "end": v(-17, 2.82) * mm});
            skLineSegment(sketch, "E373", {"start": v(-17, 2.82) * mm, "end": v(-17.14, 2.72) * mm});
            skLineSegment(sketch, "E374", {"start": v(-17.14, 2.72) * mm, "end": v(-17.3, 2.69) * mm});
            skLineSegment(sketch, "E375", {"start": v(-15.58, 3.18) * mm, "end": v(-15.08, 2.69) * mm});
            skLineSegment(sketch, "E376", {"start": v(17.3, 4.31) * mm, "end": v(15.08, 4.31) * mm});
            skLineSegment(sketch, "E377", {"start": v(16.88, 3.82) * mm, "end": v(16.9, 3.95) * mm});
            skLineSegment(sketch, "E378", {"start": v(16.9, 3.95) * mm, "end": v(16.94, 4.08) * mm});
            skLineSegment(sketch, "E379", {"start": v(16.94, 4.08) * mm, "end": v(17, 4.18) * mm});
            skLineSegment(sketch, "E380", {"start": v(17, 4.18) * mm, "end": v(17.14, 4.28) * mm});
            skLineSegment(sketch, "E381", {"start": v(17.14, 4.28) * mm, "end": v(17.3, 4.31) * mm});
            skLineSegment(sketch, "E382", {"start": v(15.58, 3.82) * mm, "end": v(15.08, 4.31) * mm});
            skLineSegment(sketch, "E383", {"start": v(-15.08, 4.31) * mm, "end": v(-17.3, 4.31) * mm});
            skLineSegment(sketch, "E384", {"start": v(-17.3, 4.31) * mm, "end": v(-17.13, 4.27) * mm});
            skLineSegment(sketch, "E385", {"start": v(-17.13, 4.27) * mm, "end": v(-17, 4.17) * mm});
            skLineSegment(sketch, "E386", {"start": v(-17, 4.17) * mm, "end": v(-16.92, 4.05) * mm});
            skLineSegment(sketch, "E387", {"start": v(-16.92, 4.05) * mm, "end": v(-16.89, 3.92) * mm});
            skLineSegment(sketch, "E388", {"start": v(-16.89, 3.92) * mm, "end": v(-16.88, 3.82) * mm});
            skLineSegment(sketch, "E389", {"start": v(-15.08, 4.31) * mm, "end": v(-15.58, 3.82) * mm});
            skLineSegment(sketch, "E390", {"start": v(24.92, 4.31) * mm, "end": v(22.7, 4.31) * mm});
            skLineSegment(sketch, "E391", {"start": v(22.7, 4.31) * mm, "end": v(22.87, 4.27) * mm});
            skLineSegment(sketch, "E392", {"start": v(22.87, 4.27) * mm, "end": v(23, 4.17) * mm});
            skLineSegment(sketch, "E393", {"start": v(23, 4.17) * mm, "end": v(23.08, 4.05) * mm});
            skLineSegment(sketch, "E394", {"start": v(23.08, 4.05) * mm, "end": v(23.11, 3.92) * mm});
            skLineSegment(sketch, "E395", {"start": v(23.11, 3.92) * mm, "end": v(23.12, 3.82) * mm});
            skLineSegment(sketch, "E396", {"start": v(24.92, 4.31) * mm, "end": v(24.42, 3.82) * mm});
            skLineSegment(sketch, "E397", {"start": v(-22.7, 4.31) * mm, "end": v(-24.92, 4.31) * mm});
            skLineSegment(sketch, "E398", {"start": v(-23.12, 3.82) * mm, "end": v(-23.1, 3.95) * mm});
            skLineSegment(sketch, "E399", {"start": v(-23.1, 3.95) * mm, "end": v(-23.06, 4.08) * mm});
            skLineSegment(sketch, "E400", {"start": v(-23.06, 4.08) * mm, "end": v(-23, 4.18) * mm});
            skLineSegment(sketch, "E401", {"start": v(-23, 4.18) * mm, "end": v(-22.86, 4.28) * mm});
            skLineSegment(sketch, "E402", {"start": v(-22.86, 4.28) * mm, "end": v(-22.7, 4.31) * mm});
            skLineSegment(sketch, "E403", {"start": v(-24.42, 3.82) * mm, "end": v(-24.92, 4.31) * mm});
            skLineSegment(sketch, "E404", {"start": v(15.09, 30.38) * mm, "end": v(15.08, 30.37) * mm});
            skLineSegment(sketch, "E405", {"start": v(15.08, 30.37) * mm, "end": v(15.08, 30.37) * mm});
            skLineSegment(sketch, "E406", {"start": v(15.08, 32.63) * mm, "end": v(15.08, 32.62) * mm});
            skLineSegment(sketch, "E407", {"start": v(15.08, 32.62) * mm, "end": v(15.09, 32.62) * mm});
            skLineSegment(sketch, "E408", {"start": v(15.08, 30.37) * mm, "end": v(15.08, 32.63) * mm});
            skLineSegment(sketch, "E409", {"start": v(-15.08, 30.37) * mm, "end": v(-15.08, 30.38) * mm});
            skLineSegment(sketch, "E410", {"start": v(-15.08, 30.38) * mm, "end": v(-15.09, 30.38) * mm});
            skLineSegment(sketch, "E411", {"start": v(-15.08, 30.37) * mm, "end": v(-15.08, 32.63) * mm});
            skLineSegment(sketch, "E412", {"start": v(-15.09, 32.62) * mm, "end": v(-15.08, 32.63) * mm});
            skLineSegment(sketch, "E413", {"start": v(-15.08, 32.63) * mm, "end": v(-15.08, 32.63) * mm});
            skLineSegment(sketch, "E414", {"start": v(24.92, 30.37) * mm, "end": v(24.92, 32.63) * mm});
            skLineSegment(sketch, "E415", {"start": v(24.92, 30.37) * mm, "end": v(24.92, 30.38) * mm});
            skLineSegment(sketch, "E416", {"start": v(24.92, 30.38) * mm, "end": v(24.91, 30.38) * mm});
            skLineSegment(sketch, "E417", {"start": v(24.91, 32.62) * mm, "end": v(24.92, 32.63) * mm});
            skLineSegment(sketch, "E418", {"start": v(24.92, 32.63) * mm, "end": v(24.92, 32.63) * mm});
            skLineSegment(sketch, "E419", {"start": v(-24.91, 30.38) * mm, "end": v(-24.92, 30.37) * mm});
            skLineSegment(sketch, "E420", {"start": v(-24.92, 30.37) * mm, "end": v(-24.92, 30.37) * mm});
            skLineSegment(sketch, "E421", {"start": v(-24.92, 32.63) * mm, "end": v(-24.92, 32.62) * mm});
            skLineSegment(sketch, "E422", {"start": v(-24.92, 32.62) * mm, "end": v(-24.91, 32.62) * mm});
            skLineSegment(sketch, "E423", {"start": v(-24.92, 30.37) * mm, "end": v(-24.92, 32.63) * mm});
            skLineSegment(sketch, "E424", {"start": v(15.08, 2.69) * mm, "end": v(15.08, 2.68) * mm});
            skLineSegment(sketch, "E425", {"start": v(15.08, 4.32) * mm, "end": v(15.08, 4.31) * mm});
            skLineSegment(sketch, "E426", {"start": v(15.08, 2.68) * mm, "end": v(15.08, 4.32) * mm});
            skLineSegment(sketch, "E427", {"start": v(24.92, 2.68) * mm, "end": v(24.92, 4.32) * mm});
            skLineSegment(sketch, "E428", {"start": v(24.92, 2.68) * mm, "end": v(24.92, 2.69) * mm});
            skLineSegment(sketch, "E429", {"start": v(24.92, 4.31) * mm, "end": v(24.92, 4.32) * mm});
            skLineSegment(sketch, "E430", {"start": v(-15.08, 2.68) * mm, "end": v(-15.08, 2.69) * mm});
            skLineSegment(sketch, "E431", {"start": v(-15.08, 2.68) * mm, "end": v(-15.08, 4.32) * mm});
            skLineSegment(sketch, "E432", {"start": v(-15.08, 4.31) * mm, "end": v(-15.08, 4.32) * mm});
            skLineSegment(sketch, "E433", {"start": v(-24.92, 2.69) * mm, "end": v(-24.92, 2.68) * mm});
            skLineSegment(sketch, "E434", {"start": v(-24.92, 4.32) * mm, "end": v(-24.92, 4.31) * mm});
            skLineSegment(sketch, "E435", {"start": v(-24.92, 2.68) * mm, "end": v(-24.92, 4.32) * mm});
            skLineSegment(sketch, "E436", {"start": v(17.26, 30.38) * mm, "end": v(17.52, 30.34) * mm});
            skLineSegment(sketch, "E437", {"start": v(17.52, 30.34) * mm, "end": v(17.8, 30.3) * mm});
            skLineSegment(sketch, "E438", {"start": v(17.8, 30.3) * mm, "end": v(18.1, 30.27) * mm});
            skLineSegment(sketch, "E439", {"start": v(18.1, 30.27) * mm, "end": v(18.42, 30.25) * mm});
            skLineSegment(sketch, "E440", {"start": v(18.42, 30.25) * mm, "end": v(18.75, 30.22) * mm});
            skLineSegment(sketch, "E441", {"start": v(18.75, 30.22) * mm, "end": v(19.08, 30.2) * mm});
            skLineSegment(sketch, "E442", {"start": v(19.08, 30.2) * mm, "end": v(19.43, 30.2) * mm});
            skLineSegment(sketch, "E443", {"start": v(19.43, 30.2) * mm, "end": v(19.77, 30.19) * mm});
            skLineSegment(sketch, "E444", {"start": v(19.77, 30.19) * mm, "end": v(20.12, 30.19) * mm});
            skLineSegment(sketch, "E445", {"start": v(20.12, 30.19) * mm, "end": v(20.47, 30.2) * mm});
            skLineSegment(sketch, "E446", {"start": v(20.47, 30.2) * mm, "end": v(20.81, 30.2) * mm});
            skLineSegment(sketch, "E447", {"start": v(20.81, 30.2) * mm, "end": v(21.15, 30.22) * mm});
            skLineSegment(sketch, "E448", {"start": v(21.15, 30.22) * mm, "end": v(21.48, 30.24) * mm});
            skLineSegment(sketch, "E449", {"start": v(21.48, 30.24) * mm, "end": v(21.8, 30.26) * mm});
            skLineSegment(sketch, "E450", {"start": v(21.8, 30.26) * mm, "end": v(22.1, 30.3) * mm});
            skLineSegment(sketch, "E451", {"start": v(22.1, 30.3) * mm, "end": v(22.4, 30.33) * mm});
            skLineSegment(sketch, "E452", {"start": v(22.4, 30.33) * mm, "end": v(22.66, 30.37) * mm});
            skLineSegment(sketch, "E453", {"start": v(22.66, 30.37) * mm, "end": v(22.74, 30.38) * mm});
            skLineSegment(sketch, "E454", {"start": v(22.74, 32.62) * mm, "end": v(22.48, 32.66) * mm});
            skLineSegment(sketch, "E455", {"start": v(22.48, 32.66) * mm, "end": v(22.2, 32.7) * mm});
            skLineSegment(sketch, "E456", {"start": v(22.2, 32.7) * mm, "end": v(21.9, 32.73) * mm});
            skLineSegment(sketch, "E457", {"start": v(21.9, 32.73) * mm, "end": v(21.58, 32.75) * mm});
            skLineSegment(sketch, "E458", {"start": v(21.58, 32.75) * mm, "end": v(21.25, 32.78) * mm});
            skLineSegment(sketch, "E459", {"start": v(21.25, 32.78) * mm, "end": v(20.92, 32.8) * mm});
            skLineSegment(sketch, "E460", {"start": v(20.92, 32.8) * mm, "end": v(20.57, 32.8) * mm});
            skLineSegment(sketch, "E461", {"start": v(20.57, 32.8) * mm, "end": v(20.23, 32.81) * mm});
            skLineSegment(sketch, "E462", {"start": v(20.23, 32.81) * mm, "end": v(19.88, 32.81) * mm});
            skLineSegment(sketch, "E463", {"start": v(19.88, 32.81) * mm, "end": v(19.53, 32.8) * mm});
            skLineSegment(sketch, "E464", {"start": v(19.53, 32.8) * mm, "end": v(19.19, 32.8) * mm});
            skLineSegment(sketch, "E465", {"start": v(19.19, 32.8) * mm, "end": v(18.85, 32.78) * mm});
            skLineSegment(sketch, "E466", {"start": v(18.85, 32.78) * mm, "end": v(18.52, 32.76) * mm});
            skLineSegment(sketch, "E467", {"start": v(18.52, 32.76) * mm, "end": v(18.2, 32.74) * mm});
            skLineSegment(sketch, "E468", {"start": v(18.2, 32.74) * mm, "end": v(17.9, 32.7) * mm});
            skLineSegment(sketch, "E469", {"start": v(17.9, 32.7) * mm, "end": v(17.6, 32.67) * mm});
            skLineSegment(sketch, "E470", {"start": v(17.6, 32.67) * mm, "end": v(17.34, 32.63) * mm});
            skLineSegment(sketch, "E471", {"start": v(17.34, 32.63) * mm, "end": v(17.26, 32.62) * mm});
            skLineSegment(sketch, "E472", {"start": v(17.3, 2.69) * mm, "end": v(17.57, 2.67) * mm});
            skLineSegment(sketch, "E473", {"start": v(17.57, 2.67) * mm, "end": v(17.86, 2.65) * mm});
            skLineSegment(sketch, "E474", {"start": v(17.86, 2.65) * mm, "end": v(18.16, 2.63) * mm});
            skLineSegment(sketch, "E475", {"start": v(18.16, 2.63) * mm, "end": v(18.48, 2.62) * mm});
            skLineSegment(sketch, "E476", {"start": v(18.48, 2.62) * mm, "end": v(18.8, 2.6) * mm});
            skLineSegment(sketch, "E477", {"start": v(18.8, 2.6) * mm, "end": v(19.14, 2.6) * mm});
            skLineSegment(sketch, "E478", {"start": v(19.14, 2.6) * mm, "end": v(19.49, 2.6) * mm});
            skLineSegment(sketch, "E479", {"start": v(19.49, 2.6) * mm, "end": v(19.84, 2.6) * mm});
            skLineSegment(sketch, "E480", {"start": v(19.84, 2.6) * mm, "end": v(20.19, 2.6) * mm});
            skLineSegment(sketch, "E481", {"start": v(20.19, 2.6) * mm, "end": v(20.53, 2.6) * mm});
            skLineSegment(sketch, "E482", {"start": v(20.53, 2.6) * mm, "end": v(20.88, 2.6) * mm});
            skLineSegment(sketch, "E483", {"start": v(20.88, 2.6) * mm, "end": v(21.21, 2.61) * mm});
            skLineSegment(sketch, "E484", {"start": v(21.21, 2.61) * mm, "end": v(21.54, 2.62) * mm});
            skLineSegment(sketch, "E485", {"start": v(21.54, 2.62) * mm, "end": v(21.86, 2.63) * mm});
            skLineSegment(sketch, "E486", {"start": v(21.86, 2.63) * mm, "end": v(22.16, 2.65) * mm});
            skLineSegment(sketch, "E487", {"start": v(22.16, 2.65) * mm, "end": v(22.44, 2.67) * mm});
            skLineSegment(sketch, "E488", {"start": v(22.44, 2.67) * mm, "end": v(22.7, 2.69) * mm});
            skLineSegment(sketch, "E489", {"start": v(22.7, 4.31) * mm, "end": v(22.43, 4.33) * mm});
            skLineSegment(sketch, "E490", {"start": v(22.43, 4.33) * mm, "end": v(22.14, 4.35) * mm});
            skLineSegment(sketch, "E491", {"start": v(22.14, 4.35) * mm, "end": v(21.84, 4.37) * mm});
            skLineSegment(sketch, "E492", {"start": v(21.84, 4.37) * mm, "end": v(21.52, 4.38) * mm});
            skLineSegment(sketch, "E493", {"start": v(21.52, 4.38) * mm, "end": v(21.2, 4.4) * mm});
            skLineSegment(sketch, "E494", {"start": v(21.2, 4.4) * mm, "end": v(20.86, 4.4) * mm});
            skLineSegment(sketch, "E495", {"start": v(20.86, 4.4) * mm, "end": v(20.51, 4.4) * mm});
            skLineSegment(sketch, "E496", {"start": v(20.51, 4.4) * mm, "end": v(20.16, 4.4) * mm});
            skLineSegment(sketch, "E497", {"start": v(20.16, 4.4) * mm, "end": v(19.81, 4.4) * mm});
            skLineSegment(sketch, "E498", {"start": v(19.81, 4.4) * mm, "end": v(19.47, 4.4) * mm});
            skLineSegment(sketch, "E499", {"start": v(19.47, 4.4) * mm, "end": v(19.12, 4.4) * mm});
            skLineSegment(sketch, "E500", {"start": v(19.12, 4.4) * mm, "end": v(18.79, 4.39) * mm});
            skLineSegment(sketch, "E501", {"start": v(18.79, 4.39) * mm, "end": v(18.46, 4.38) * mm});
            skLineSegment(sketch, "E502", {"start": v(18.46, 4.38) * mm, "end": v(18.14, 4.37) * mm});
            skLineSegment(sketch, "E503", {"start": v(18.14, 4.37) * mm, "end": v(17.84, 4.35) * mm});
            skLineSegment(sketch, "E504", {"start": v(17.84, 4.35) * mm, "end": v(17.56, 4.33) * mm});
            skLineSegment(sketch, "E505", {"start": v(17.56, 4.33) * mm, "end": v(17.3, 4.31) * mm});
            skLineSegment(sketch, "E506", {"start": v(-22.74, 30.38) * mm, "end": v(-22.48, 30.34) * mm});
            skLineSegment(sketch, "E507", {"start": v(-22.48, 30.34) * mm, "end": v(-22.2, 30.3) * mm});
            skLineSegment(sketch, "E508", {"start": v(-22.2, 30.3) * mm, "end": v(-21.9, 30.27) * mm});
            skLineSegment(sketch, "E509", {"start": v(-21.9, 30.27) * mm, "end": v(-21.58, 30.25) * mm});
            skLineSegment(sketch, "E510", {"start": v(-21.58, 30.25) * mm, "end": v(-21.25, 30.22) * mm});
            skLineSegment(sketch, "E511", {"start": v(-21.25, 30.22) * mm, "end": v(-20.92, 30.2) * mm});
            skLineSegment(sketch, "E512", {"start": v(-20.92, 30.2) * mm, "end": v(-20.57, 30.2) * mm});
            skLineSegment(sketch, "E513", {"start": v(-20.57, 30.2) * mm, "end": v(-20.23, 30.19) * mm});
            skLineSegment(sketch, "E514", {"start": v(-20.23, 30.19) * mm, "end": v(-19.88, 30.19) * mm});
            skLineSegment(sketch, "E515", {"start": v(-19.88, 30.19) * mm, "end": v(-19.53, 30.2) * mm});
            skLineSegment(sketch, "E516", {"start": v(-19.53, 30.2) * mm, "end": v(-19.19, 30.2) * mm});
            skLineSegment(sketch, "E517", {"start": v(-19.19, 30.2) * mm, "end": v(-18.85, 30.22) * mm});
            skLineSegment(sketch, "E518", {"start": v(-18.85, 30.22) * mm, "end": v(-18.52, 30.24) * mm});
            skLineSegment(sketch, "E519", {"start": v(-18.52, 30.24) * mm, "end": v(-18.2, 30.26) * mm});
            skLineSegment(sketch, "E520", {"start": v(-18.2, 30.26) * mm, "end": v(-17.9, 30.3) * mm});
            skLineSegment(sketch, "E521", {"start": v(-17.9, 30.3) * mm, "end": v(-17.6, 30.33) * mm});
            skLineSegment(sketch, "E522", {"start": v(-17.6, 30.33) * mm, "end": v(-17.34, 30.37) * mm});
            skLineSegment(sketch, "E523", {"start": v(-17.34, 30.37) * mm, "end": v(-17.26, 30.38) * mm});
            skLineSegment(sketch, "E524", {"start": v(-17.26, 32.62) * mm, "end": v(-17.52, 32.66) * mm});
            skLineSegment(sketch, "E525", {"start": v(-17.52, 32.66) * mm, "end": v(-17.8, 32.7) * mm});
            skLineSegment(sketch, "E526", {"start": v(-17.8, 32.7) * mm, "end": v(-18.1, 32.73) * mm});
            skLineSegment(sketch, "E527", {"start": v(-18.1, 32.73) * mm, "end": v(-18.42, 32.75) * mm});
            skLineSegment(sketch, "E528", {"start": v(-18.42, 32.75) * mm, "end": v(-18.75, 32.78) * mm});
            skLineSegment(sketch, "E529", {"start": v(-18.75, 32.78) * mm, "end": v(-19.08, 32.8) * mm});
            skLineSegment(sketch, "E530", {"start": v(-19.08, 32.8) * mm, "end": v(-19.43, 32.8) * mm});
            skLineSegment(sketch, "E531", {"start": v(-19.43, 32.8) * mm, "end": v(-19.77, 32.81) * mm});
            skLineSegment(sketch, "E532", {"start": v(-19.77, 32.81) * mm, "end": v(-20.12, 32.81) * mm});
            skLineSegment(sketch, "E533", {"start": v(-20.12, 32.81) * mm, "end": v(-20.47, 32.8) * mm});
            skLineSegment(sketch, "E534", {"start": v(-20.47, 32.8) * mm, "end": v(-20.81, 32.8) * mm});
            skLineSegment(sketch, "E535", {"start": v(-20.81, 32.8) * mm, "end": v(-21.15, 32.78) * mm});
            skLineSegment(sketch, "E536", {"start": v(-21.15, 32.78) * mm, "end": v(-21.48, 32.76) * mm});
            skLineSegment(sketch, "E537", {"start": v(-21.48, 32.76) * mm, "end": v(-21.8, 32.74) * mm});
            skLineSegment(sketch, "E538", {"start": v(-21.8, 32.74) * mm, "end": v(-22.1, 32.7) * mm});
            skLineSegment(sketch, "E539", {"start": v(-22.1, 32.7) * mm, "end": v(-22.4, 32.67) * mm});
            skLineSegment(sketch, "E540", {"start": v(-22.4, 32.67) * mm, "end": v(-22.66, 32.63) * mm});
            skLineSegment(sketch, "E541", {"start": v(-22.66, 32.63) * mm, "end": v(-22.74, 32.62) * mm});
            skLineSegment(sketch, "E542", {"start": v(-22.7, 2.69) * mm, "end": v(-22.43, 2.67) * mm});
            skLineSegment(sketch, "E543", {"start": v(-22.43, 2.67) * mm, "end": v(-22.14, 2.65) * mm});
            skLineSegment(sketch, "E544", {"start": v(-22.14, 2.65) * mm, "end": v(-21.84, 2.63) * mm});
            skLineSegment(sketch, "E545", {"start": v(-21.84, 2.63) * mm, "end": v(-21.52, 2.62) * mm});
            skLineSegment(sketch, "E546", {"start": v(-21.52, 2.62) * mm, "end": v(-21.2, 2.6) * mm});
            skLineSegment(sketch, "E547", {"start": v(-21.2, 2.6) * mm, "end": v(-20.86, 2.6) * mm});
            skLineSegment(sketch, "E548", {"start": v(-20.86, 2.6) * mm, "end": v(-20.51, 2.6) * mm});
            skLineSegment(sketch, "E549", {"start": v(-20.51, 2.6) * mm, "end": v(-20.16, 2.6) * mm});
            skLineSegment(sketch, "E550", {"start": v(-20.16, 2.6) * mm, "end": v(-19.81, 2.6) * mm});
            skLineSegment(sketch, "E551", {"start": v(-19.81, 2.6) * mm, "end": v(-19.47, 2.6) * mm});
            skLineSegment(sketch, "E552", {"start": v(-19.47, 2.6) * mm, "end": v(-19.12, 2.6) * mm});
            skLineSegment(sketch, "E553", {"start": v(-19.12, 2.6) * mm, "end": v(-18.79, 2.61) * mm});
            skLineSegment(sketch, "E554", {"start": v(-18.79, 2.61) * mm, "end": v(-18.46, 2.62) * mm});
            skLineSegment(sketch, "E555", {"start": v(-18.46, 2.62) * mm, "end": v(-18.14, 2.63) * mm});
            skLineSegment(sketch, "E556", {"start": v(-18.14, 2.63) * mm, "end": v(-17.84, 2.65) * mm});
            skLineSegment(sketch, "E557", {"start": v(-17.84, 2.65) * mm, "end": v(-17.56, 2.67) * mm});
            skLineSegment(sketch, "E558", {"start": v(-17.56, 2.67) * mm, "end": v(-17.3, 2.69) * mm});
            skLineSegment(sketch, "E559", {"start": v(-17.3, 4.31) * mm, "end": v(-17.57, 4.33) * mm});
            skLineSegment(sketch, "E560", {"start": v(-17.57, 4.33) * mm, "end": v(-17.86, 4.35) * mm});
            skLineSegment(sketch, "E561", {"start": v(-17.86, 4.35) * mm, "end": v(-18.16, 4.37) * mm});
            skLineSegment(sketch, "E562", {"start": v(-18.16, 4.37) * mm, "end": v(-18.48, 4.38) * mm});
            skLineSegment(sketch, "E563", {"start": v(-18.48, 4.38) * mm, "end": v(-18.8, 4.4) * mm});
            skLineSegment(sketch, "E564", {"start": v(-18.8, 4.4) * mm, "end": v(-19.14, 4.4) * mm});
            skLineSegment(sketch, "E565", {"start": v(-19.14, 4.4) * mm, "end": v(-19.49, 4.4) * mm});
            skLineSegment(sketch, "E566", {"start": v(-19.49, 4.4) * mm, "end": v(-19.84, 4.4) * mm});
            skLineSegment(sketch, "E567", {"start": v(-19.84, 4.4) * mm, "end": v(-20.19, 4.4) * mm});
            skLineSegment(sketch, "E568", {"start": v(-20.19, 4.4) * mm, "end": v(-20.53, 4.4) * mm});
            skLineSegment(sketch, "E569", {"start": v(-20.53, 4.4) * mm, "end": v(-20.88, 4.4) * mm});
            skLineSegment(sketch, "E570", {"start": v(-20.88, 4.4) * mm, "end": v(-21.21, 4.39) * mm});
            skLineSegment(sketch, "E571", {"start": v(-21.21, 4.39) * mm, "end": v(-21.54, 4.38) * mm});
            skLineSegment(sketch, "E572", {"start": v(-21.54, 4.38) * mm, "end": v(-21.86, 4.37) * mm});
            skLineSegment(sketch, "E573", {"start": v(-21.86, 4.37) * mm, "end": v(-22.16, 4.35) * mm});
            skLineSegment(sketch, "E574", {"start": v(-22.16, 4.35) * mm, "end": v(-22.44, 4.33) * mm});
            skLineSegment(sketch, "E575", {"start": v(-22.44, 4.33) * mm, "end": v(-22.7, 4.31) * mm});
            skLineSegment(sketch, "E576", {"start": v(-25, 30.1) * mm, "end": v(-25, 32.9) * mm});
            skLineSegment(sketch, "E577", {"start": v(-25, 30.1) * mm, "end": v(-24.92, 30.37) * mm});
            skLineSegment(sketch, "E578", {"start": v(-24.92, 32.63) * mm, "end": v(-25, 32.9) * mm});
            skLineSegment(sketch, "E579", {"start": v(15, 30.1) * mm, "end": v(15, 32.9) * mm});
            skLineSegment(sketch, "E580", {"start": v(15, 30.1) * mm, "end": v(15.08, 30.37) * mm});
            skLineSegment(sketch, "E581", {"start": v(15.08, 32.63) * mm, "end": v(15, 32.9) * mm});
            skLineSegment(sketch, "E582", {"start": v(-15, 32.9) * mm, "end": v(-25, 32.9) * mm});
            skLineSegment(sketch, "E583", {"start": v(-15, 32.9) * mm, "end": v(-15.08, 32.63) * mm});
            skLineSegment(sketch, "E584", {"start": v(25, 32.9) * mm, "end": v(15, 32.9) * mm});
            skLineSegment(sketch, "E585", {"start": v(25, 32.9) * mm, "end": v(24.92, 32.63) * mm});
            skLineSegment(sketch, "E586", {"start": v(-15, 30.1) * mm, "end": v(-15, 32.9) * mm});
            skLineSegment(sketch, "E587", {"start": v(-15.08, 30.37) * mm, "end": v(-15, 30.1) * mm});
            skLineSegment(sketch, "E588", {"start": v(-15, 30.1) * mm, "end": v(-25, 30.1) * mm});
            skLineSegment(sketch, "E589", {"start": v(25, 30.1) * mm, "end": v(15, 30.1) * mm});
            skLineSegment(sketch, "E590", {"start": v(24.92, 30.37) * mm, "end": v(25, 30.1) * mm});
            skLineSegment(sketch, "E591", {"start": v(25, 30.1) * mm, "end": v(25, 32.9) * mm});
            skLineSegment(sketch, "E592", {"start": v(-25, 2.55) * mm, "end": v(-25, 4.45) * mm});
            skLineSegment(sketch, "E593", {"start": v(-25, 2.55) * mm, "end": v(-24.92, 2.68) * mm});
            skLineSegment(sketch, "E594", {"start": v(-24.92, 4.32) * mm, "end": v(-25, 4.45) * mm});
            skLineSegment(sketch, "E595", {"start": v(15, 2.55) * mm, "end": v(15, 4.45) * mm});
            skLineSegment(sketch, "E596", {"start": v(15, 2.55) * mm, "end": v(15.08, 2.68) * mm});
            skLineSegment(sketch, "E597", {"start": v(15.08, 4.32) * mm, "end": v(15, 4.45) * mm});
            skLineSegment(sketch, "E598", {"start": v(25, 4.45) * mm, "end": v(15, 4.45) * mm});
            skLineSegment(sketch, "E599", {"start": v(25, 4.45) * mm, "end": v(24.92, 4.32) * mm});
            skLineSegment(sketch, "E600", {"start": v(-15, 4.45) * mm, "end": v(-25, 4.45) * mm});
            skLineSegment(sketch, "E601", {"start": v(-15, 4.45) * mm, "end": v(-15.08, 4.32) * mm});
            skLineSegment(sketch, "E602", {"start": v(-15, 2.55) * mm, "end": v(-15, 4.45) * mm});
            skLineSegment(sketch, "E603", {"start": v(-15.08, 2.68) * mm, "end": v(-15, 2.55) * mm});
            skLineSegment(sketch, "E604", {"start": v(25, 2.55) * mm, "end": v(15, 2.55) * mm});
            skLineSegment(sketch, "E605", {"start": v(24.92, 2.68) * mm, "end": v(25, 2.55) * mm});
            skLineSegment(sketch, "E606", {"start": v(25, 2.55) * mm, "end": v(25, 4.45) * mm});
            skLineSegment(sketch, "E607", {"start": v(-15, 2.55) * mm, "end": v(-25, 2.55) * mm});
            skLineSegment(sketch, "E608", {"start": v(-15.9, 31) * mm, "end": v(-15.9, 40) * mm});
            skLineSegment(sketch, "E609", {"start": v(-24.1, 40) * mm, "end": v(-24.1, 31) * mm});
            skLineSegment(sketch, "E610", {"start": v(24.1, 31) * mm, "end": v(24.1, 40) * mm});
            skLineSegment(sketch, "E611", {"start": v(15.9, 40) * mm, "end": v(15.9, 31) * mm});
            skLineSegment(sketch, "E612", {"start": v(-24.3, 10) * mm, "end": v(-15.7, 10) * mm, "construction": true});
            skLineSegment(sketch, "E613", {"start": v(-20, 5.7) * mm, "end": v(-20, 14.3) * mm, "construction": true});
            skLineSegment(sketch, "E614", {"start": v(15.7, 10) * mm, "end": v(24.3, 10) * mm, "construction": true});
            skLineSegment(sketch, "E615", {"start": v(20, 5.7) * mm, "end": v(20, 14.3) * mm, "construction": true});
            skLineSegment(sketch, "E616", {"start": v(20, 40.45) * mm, "end": v(20, 30.55) * mm});
            skLineSegment(sketch, "E617", {"start": v(-20, 40.45) * mm, "end": v(-20, 30.55) * mm});
            skLineSegment(sketch, "E618", {"start": v(35, 0) * mm, "end": v(-35, 0) * mm});
            skCircle(sketch, "E619", {"center": v(-20, 10) * mm, "radius": 4.1 * mm});
            skCircle(sketch, "E620", {"center": v(20, 10) * mm, "radius": 4.1 * mm});
            skLineSegment(sketch, "E621", {"start": v(31, 0.83) * mm, "end": v(31, 31) * mm});
            skLineSegment(sketch, "E622", {"start": v(31, 0.83) * mm, "end": v(-31, 0.83) * mm});
            skLineSegment(sketch, "E623", {"start": v(-31, 0.83) * mm, "end": v(-31, 31) * mm});
            skLineSegment(sketch, "E624", {"start": v(-31, 31) * mm, "end": v(31, 31) * mm});
            skLineSegment(sketch, "E625", {"start": v(35, 0.67) * mm, "end": v(-35, 0.67) * mm});
            skLineSegment(sketch, "E626", {"start": v(35, 40) * mm, "end": v(35, 0) * mm});
            skLineSegment(sketch, "E627", {"start": v(-35, 40) * mm, "end": v(-35, 0) * mm});
            skLineSegment(sketch, "E628", {"start": v(35, 40) * mm, "end": v(-35, 40) * mm});
            skLineSegment(sketch, "E629", {"start": v(35, 31.06) * mm, "end": v(-35, 31.06) * mm});
            skLineSegment(sketch, "E630", {"start": v(35, 32) * mm, "end": v(-35, 32) * mm});
            skSolve(sketch);
        }
        {
            var Q0;
            Q0=makeQuery(id+"F5.imprint","IMPRINT",FACE,{"disambiguationData":[TD([[makeQuery(id+"F5.imprint","IMPRINT",EDGE,{"derivedFrom":sQuery(id+"F5.wireOp",EDGE,"E619")}),-1.0]])]});
            var Q1;
            Q1=makeQuery(id+"F5.imprint","IMPRINT",FACE,{"disambiguationData":[TD([[makeQuery(id+"F5.imprint","IMPRINT",EDGE,{"derivedFrom":sQuery(id+"F5.wireOp",EDGE,"E620")}),-1.0]])]});
            var Q2;
            Q2=sQuery(id+"F5.wireOp",EDGE,"E613");
            var Q3;
            Q3=sQuery(id+"F5.wireOp",EDGE,"E612");
            var Q4;
            Q4=sQuery(id+"F5.wireOp",EDGE,"E615");
            var Q5;
            Q5=sQuery(id+"F5.wireOp",EDGE,"E614");
            extrude(context, id + "F6", {"entities" : qUnion([Q0, Q1]), "operationType" : NewBodyOperationType.REMOVE, "surfaceEntities" : qUnion([Q2, Q3, Q4, Q5]), "endBound" : BoundingType.THROUGH_ALL, "oppositeDirection" : true, "depth" : 25 * mm, "offsetDistance" : 25 * mm});
        }
    });
